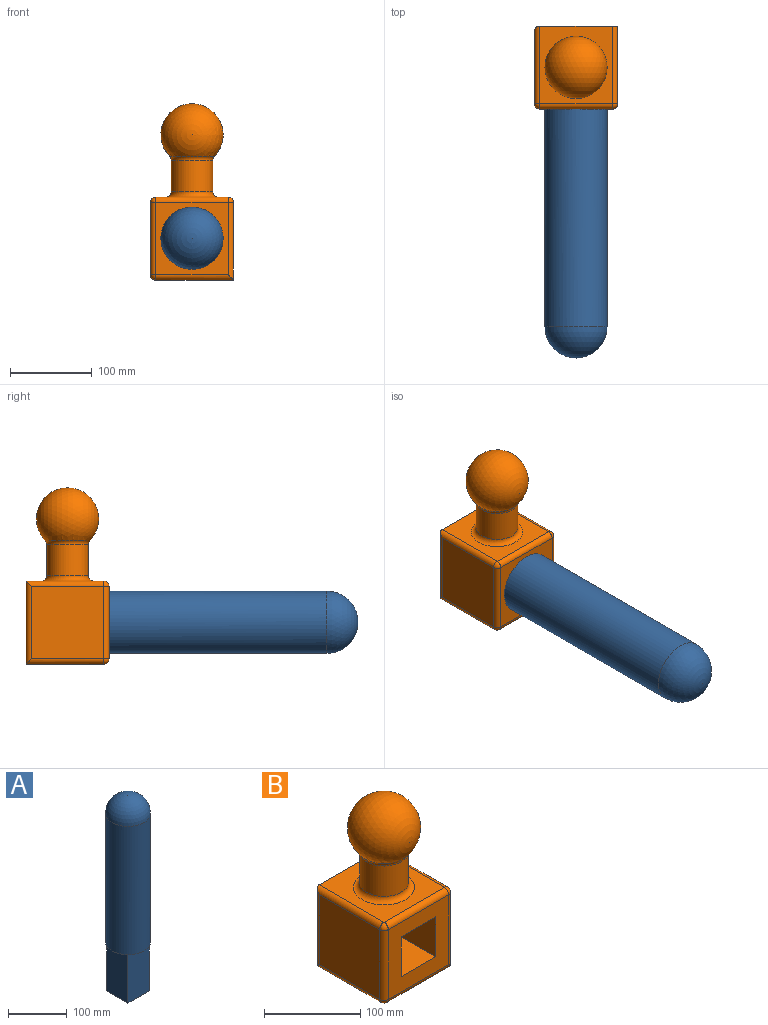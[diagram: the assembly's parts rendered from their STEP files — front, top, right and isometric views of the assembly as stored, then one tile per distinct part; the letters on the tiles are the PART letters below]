
ASSEMBLY  parts=2 mates=1
PART A: 8 faces, bbox 76.2x76.2x406.4 mm
  f0: plane 101.6x50.8mm, normal (1,0,0), area 5161.3mm2, adj f1,f3,f4,f6
  f1: plane 101.6x50.8mm, normal (0,1,0), area 5161.3mm2, adj f0,f2,f4,f6
  f2: plane 101.6x50.8mm, normal (-1,0,0), area 5161.3mm2, adj f1,f3,f4,f6
  f3: plane 101.6x50.8mm, normal (0,-1,0), area 5161.3mm2, adj f0,f2,f4,f6
  f4: plane 50.8x50.8mm, normal (0,0,-1), area 2580.6mm2, adj f0,f1,f2,f3
  f5: cylinder r=38.1mm len=266.7mm, axis (0,0,-1), area 63845.1mm2, adj f6,f7
  f6: plane 76.2x76.2mm, normal (0,0,-1), area 1979.7mm2, adj f0,f1,f2,f3,f5
  f7: sphere r=38.1mm, area 9120.7mm2, adj f5
PART B: 25 faces, bbox 101.6x101.6x215.9 mm
  f0: plane 101.6x95.25mm, normal (0,1,0), area 7088.1mm2, adj f4,f5,f6,f8,f9,f10,f11,f14
  f1: plane 88.9x88.9mm, normal (0,-1,0), area 5322.6mm2, adj f8,f9,f10,f11,f16,f17,f18,f19
  f2: cylinder r=25.4mm len=50.8mm, axis (0,0,-1), area 6182.9mm2, adj f12,f13
  f3: plane 88.9x88.9mm, normal (-1,0,0), area 7903.2mm2, adj f18,f22,f23,f24
  f4: plane 95.25x95.25mm, normal (1,0,0), area 9072.6mm2, adj f0,f6,f14,f16
  f5: plane 95.25x88.9mm, normal (0,0,1), area 5300.8mm2, adj f0,f13,f14,f17,f22
  f6: plane 95.25x95.25mm, normal (0,0,-1), area 9072.6mm2, adj f0,f4,f19,f23
  f7: sphere r=38.1mm, area 15503.9mm2, adj f12
  f8: plane 101.6x50.8mm, normal (0,0,-1), area 5161.3mm2, adj f0,f1,f9,f11
  f9: plane 101.6x50.8mm, normal (1,0,0), area 5161.3mm2, adj f0,f1,f8,f10
  f10: plane 101.6x50.8mm, normal (0,0,1), area 5161.3mm2, adj f0,f1,f9,f11
  f11: plane 101.6x50.8mm, normal (-1,0,0), area 5161.3mm2, adj f0,f1,f8,f10
  f12: torus R=31.75mm, axis (0,0,1), area 804.7mm2, adj f2,f7
  f13: torus R=31.75mm, axis (0,0,1), area 1736.5mm2, adj f2,f5
  f14: cylinder r=6.35mm len=95.25mm, axis (0,-1,0), area 950.1mm2, adj f0,f4,f5,f15
  f15: sphere r=6.35mm, area 63.3mm2, adj f14,f16,f17
  f16: cylinder r=6.35mm len=95.25mm, axis (0,0,1), area 927.1mm2, adj f1,f4,f15,f19
  f17: cylinder r=6.35mm len=88.9mm, axis (-1,0,0), area 886.7mm2, adj f1,f5,f15,f20
  f18: cylinder r=6.35mm len=88.9mm, axis (0,0,-1), area 886.7mm2, adj f1,f3,f20,f21
  f19: cylinder r=6.35mm len=95.25mm, axis (1,0,0), area 927.1mm2, adj f1,f6,f16,f21
  f20: sphere r=6.35mm, area 63.3mm2, adj f17,f18,f22
  f21: sphere r=6.35mm, area 63.3mm2, adj f18,f19,f23
  f22: cylinder r=6.35mm len=95.25mm, axis (0,1,0), area 927.1mm2, adj f3,f5,f20,f24
  f23: cylinder r=6.35mm len=95.25mm, axis (0,-1,0), area 927.1mm2, adj f3,f6,f21,f24
  f24: cylinder r=6.35mm len=101.6mm, axis (0,0,1), area 967.4mm2, adj f0,f3,f22,f23
PLACE A rot(axis=(0.58,-0.58,0.58),120deg) t=(-25.15,107.13,49.6)mm
PLACE B t=(-25.15,56.33,-1.67)mm fixed
MATE fastened A.f1 <-> B.f9  axis (-1,0,0) through (-50.55,56.33,49.6)mm
